# Revit family: LAMP_PUZZLE IND
name_source: partatom
category: Modelos genéricos
revit_build: Autodesk Revit 2015 (Build: 20140606_1530(x64)
units: mm (PartAtom-declared; Revit-internal decimal feet)

## types (32) — shared parameters
CRI = 80
Comentarios de tipo = Availability of tilting between -25º and 25º in both directions when placed in a project.
Dimensions = 140 x 140 x 139
Elevación por defecto = 1219 mm
Fabricante = LAMP
Gear = Electronic
Height = 139 mm  [stored 0.456037 ft]
Installation instructions = http://www.lamp.es
Insulation class = II
Lamp = COB LED
Last update = 24/07/2018
Luminaire type = Indoor - Recesses luminaire
MacAdam = 3
Manufacturer URL = http://www.lamp.es
Manufacturer country = Spain
Manufacturer name = LAMP
Model explanation = Availability of tilting between -25º and 25º in both directions when placed in a project.
Power Supply = 220-240V 50-60Hz
Product URL = http://www.lamp.es
Product datasheet = http://www.lamp.es
Protection rating = IP20
Type = COB PHILIPS

## per-type parameters (varying)
| type | Descripción | Efficacy | Finish | IEE | Initial color | Initial intensity | LED Lifetime | Material caja | Modelo | Photometric web file | Plum | Power | Product code | Weight |
| 1405LM 3000 BLACK FLOOD | PUZZLE G2 IND 1500 WW FL BK. | 145 lm/W | Matte black | A++ | 3000 K | 1405 lm | 50.000 L90 B10 | LAMP_Aluminio aro Puzzle BL | PU2RE115FL830NB | Aro exterior : 1405LM 3000 BLACK FLOOD | 10 W | 8 W | PU2RE115FL830NB | 1.09 kg |
| 1405LM 3000 WHITE FLOOD | PUZZLE G2 IND 1500 WW FL WH. | 145 lm/W | Matte white | A++ | 3000 K | 1405 lm | 50.000 L90 B10 | LAMP_Aluminio aro Puzzle WH | PU2RE115FL830NW | Aro exterior : 1405LM 3000 WHITE FLOOD | 10 W | 8 W | PU2RE115FL830NW | 1.09 kg |
| 1421LM 3000 BLACK MEDIUM FLOOD | PUZZLE G2 IND 1500 WW MFL BK. | 147 lm/W | Matte black | A++ | 3000 K | 1421 lm | 50.000 L90 B10 | LAMP_Aluminio aro Puzzle BL | PU2RE115MF830NB | Aro exterior : 1421LM 3000 BLACK MEDIUM FLOOD | 10 W | 8 W | PU2RE115MF830NB | 1.09 kg |
| 1421LM 3000 WHITE MEDIUM FLOOD | PUZZLE G2 IND 1500 WW MFL WH. | 147 lm/W | Matte white | A++ | 3000 K | 1421 lm | 50.000 L90 B10 | LAMP_Aluminio aro Puzzle WH | PU2RE115MF830NW | Aro exterior : 1421LM 3000 WHITE MEDIUM FLOOD | 10 W | 8 W | PU2RE115MF830NW | 1.09 kg |
| 1464LM 4000 BLACK FLOOD | PUZZLE G2 IND 1500 NW FL BK. | 151 lm/W | Matte black | A++ | 4000 K | 1464 lm | 50.000 L90 B10 | LAMP_Aluminio aro Puzzle BL | PU2RE115FL840NB | Aro exterior : 1464LM 4000 BLACK FLOOD | 10 W | 8 W | PU2RE115FL840NB | 1.09 kg |
| 1464LM 4000 WHITE FLOOD | PUZZLE G2 IND 1500 NW FL WH. | 151 lm/W | Matte white | A++ | 4000 K | 1464 lm | 50.000 L90 B10 | LAMP_Aluminio aro Puzzle WH | PU2RE115FL840NW | Aro exterior : 1464LM 4000 WHITE FLOOD | 10 W | 8 W | PU2RE115FL840NW | 1.09 kg |
| 1480LM 4000 BLACK MEDIUM FLOOD | PUZZLE G2 IND 1500 NW MFL BK. | 153 lm/W | Matte black | A++ | 4000 K | 1480 lm | 50.000 L90 B10 | LAMP_Aluminio aro Puzzle BL | PU2RE115MF840NB | Aro exterior : 1480LM 4000 BLACK MEDIUM FLOOD | 10 W | 8 W | PU2RE115MF840NB | 1.09 kg |
| 1480LM 4000 WHITE MEDIUM FLOOD | PUZZLE G2 IND 1500 NW MFL WH. | 153 lm/W | Matte white | A++ | 4000 K | 1480 lm | 50.000 L90 B10 | LAMP_Aluminio aro Puzzle WH | PU2RE115MF840NW | Aro exterior : 1480LM 4000 WHITE MEDIUM FLOOD | 10 W | 8 W | PU2RE115MF840NW | 1.09 kg |
| 2344LM 3000 BLACK FLOOD | PUZZLE G2 IND 2500 WW FL BK. | 124 lm/W | Matte black | A++ | 3000 K | 2344 lm | 50.000 L80 B10 | LAMP_Aluminio aro Puzzle BL | PU2RE125FL830NB | Aro exterior : 2344LM 3000 BLACK FLOOD | 19 W | 18 W | PU2RE125FL830NB | 1.09 kg |
| 2344LM 3000 WHITE FLOOD | PUZZLE G2 IND 2500 WW FL WH. | 124 lm/W | Matte white | A++ | 3000 K | 2344 lm | 50.000 L80 B10 | LAMP_Aluminio aro Puzzle WH | PU2RE125FL830NW | Aro exterior : 2344LM 3000 WHITE FLOOD | 19 W | 18 W | PU2RE125FL830NW | 1.09 kg |
| 2368LM 3000 BLACK MEDIUM FLOOD | PUZZLE G2 IND 2500 WW MFL BK. | 125 lm/W | Matte black | A++ | 3000 K | 2368 lm | 50.000 L80 B10 | LAMP_Aluminio aro Puzzle BL | PU2RE125MF830NB | Aro exterior : 2368LM 3000 BLACK MEDIUM FLOOD | 19 W | 18 W | PU2RE125MF830NB | 1.09 kg |
| 2368LM 3000 WHITE MEDIUM FLOOD | PUZZLE G2 IND 2500 WW MFL WH. | 125 lm/W | Matte white | A++ | 3000 K | 2368 lm | 50.000 L80 B10 | LAMP_Aluminio aro Puzzle WH | PU2RE125MF830NW | Aro exterior : 2368LM 3000 WHITE MEDIUM FLOOD | 19 W | 18 W | PU2RE125MF830NW | 1.09 kg |
| 2442LM 4000 BLACK FLOOD | PUZZLE G2 IND 2500 NW FL BK. | 129 lm/W | Matte black | A++ | 4000 K | 2442 lm | 50.000 L80 B10 | LAMP_Aluminio aro Puzzle BL | PU2RE125FL840NB | Aro exterior : 2442LM 4000 BLACK FLOOD | 19 W | 18 W | PU2RE125FL840NB | 1.09 kg |
| 2442LM 4000 WHITE FLOOD | PUZZLE G2 IND 2500 NW FL WH. | 129 lm/W | Matte white | A++ | 4000 K | 2442 lm | 50.000 L80 B10 | LAMP_Aluminio aro Puzzle WH | PU2RE125FL840NW | Aro exterior : 2442LM 4000 WHITE FLOOD | 19 W | 18 W | PU2RE125FL840NW | 1.09 kg |
| 2466LM 4000 BLACK MEDIUM FLOOD | PUZZLE G2 IND 2500 NW MFL BK. | 131 lm/W | Matte black | A++ | 4000 K | 2466 lm | 50.000 L80 B10 | LAMP_Aluminio aro Puzzle BL | PU2RE125MF840NB | Aro exterior : 2466LM 4000 BLACK MEDIUM FLOOD | 19 W | 18 W | PU2RE125MF840NB | 1.09 kg |
| 2466LM 4000 WHITE MEDIUM FLOOD | PUZZLE G2 IND 2500 NW MFL WH. | 131 lm/W | Matte white | A++ | 4000 K | 2466 lm | 50.000 L80 B10 | LAMP_Aluminio aro Puzzle WH | PU2RE125MF840NW | Aro exterior : 2466LM 4000 WHITE MEDIUM FLOOD | 19 W | 18 W | PU2RE125MF840NW | 1.09 kg |
| 3197LM 3000 BLACK FLOOD | PUZZLE G2 IND 3500 WW FL BK. | 97 lm/W | Matte black | A+ | 3000 K | 3197 lm | 50.000 L70 B10 | LAMP_Aluminio aro Puzzle BL | PU2RE135FL830NB | Aro exterior : 3197LM 3000 BLACK FLOOD | 33 W | 27 W | PU2RE135FL830NB | 1.14 kg |
| 3197LM 3000 WHITE FLOOD | PUZZLE G2 IND 3500 WW FL WH. | 97 lm/W | Matte white | A+ | 3000 K | 3197 lm | 50.000 L70 B10 | LAMP_Aluminio aro Puzzle WH | PU2RE135FL830NW | Aro exterior : 3197LM 3000 WHITE FLOOD | 33 W | 27 W | PU2RE135FL830NW | 1.14 kg |
| 3229LM 3000 BLACK MEDIUM FLOOD | PUZZLE G2 IND 3500 WW MFL BK. | 98 lm/W | Matte black | A+ | 3000 K | 3229 lm | 50.000 L70 B10 | LAMP_Aluminio aro Puzzle BL | PU2RE135MF830NB | Aro exterior : 3229LM 3000 BLACK MEDIUM FLOOD | 33 W | 27 W | PU2RE135MF830NB | 1.14 kg |
| 3229LM 3000 WHITE MEDIUM FLOOD | PUZZLE G2 IND 3500 WW MFL WH. | 98 lm/W | Matte white | A+ | 3000 K | 3229 lm | 50.000 L70 B10 | LAMP_Aluminio aro Puzzle WH | PU2RE135MF830NW | Aro exterior : 3229LM 3000 WHITE MEDIUM FLOOD | 33 W | 27 W | PU2RE135MF830NW | 1.14 kg |
| 3330LM 4000 BLACK FLOOD | PUZZLE G2 IND 3500 NW FL BK. | 101 lm/W | Matte black | A+ | 4000 K | 3330 lm | 50.000 L70 B10 | LAMP_Aluminio aro Puzzle BL | PU2RE135FL840NB | Aro exterior : 3330LM 4000 BLACK FLOOD | 33 W | 27 W | PU2RE135FL840NB | 1.14 kg |
| 3330LM 4000 WHITE FLOOD | PUZZLE G2 IND 3500 NW FL WH. | 101 lm/W | Matte white | A+ | 4000 K | 3330 lm | 50.000 L70 B10 | LAMP_Aluminio aro Puzzle WH | PU2RE135FL840NW | Aro exterior : 3330LM 4000 WHITE FLOOD | 33 W | 27 W | PU2RE135FL840NW | 1.14 kg |
| 3363LM 4000 BLACK MEDIUM FLOOD | PUZZLE G2 IND 3500 NW MFL BK. | 102 lm/W | Matte black | A+ | 4000 K | 3363 lm | 50.000 L70 B10 | LAMP_Aluminio aro Puzzle BL | PU2RE135MF840NB | Aro exterior : 3363LM 4000 BLACK MEDIUM FLOOD | 33 W | 27 W | PU2RE135MF840NB | 1.14 kg |
| 3363LM 4000 WHITE MEDIUM FLOOD | PUZZLE G2 IND 3500 NW MFL WH. | 102 lm/W | Matte white | A+ | 4000 K | 3363 lm | 50.000 L70 B10 | LAMP_Aluminio aro Puzzle WH | PU2RE135MF840NW | Aro exterior : 3363LM 4000 WHITE MEDIUM FLOOD | 33 W | 27 W | PU2RE135MF840NW | 1.14 kg |
| 4051LM 3000 BLACK MEDIUM FLOOD | PUZZLE G2 IND 4600 WW MFL BK. | 106 lm/W | Matte black | A+ | 3000 K | 4051 lm | 50.000 L80 B10 | LAMP_Aluminio aro Puzzle BL | PU2RE145MF830NB | Aro exterior : 4051LM 3000 BLACK MEDIUM FLOOD | 38 W | 33 W | PU2RE145MF830NB | 1.22 kg |
| 4051LM 3000 WHITE MEDIUM FLOOD | PUZZLE G2 IND 4600 WW MFL WH. | 106 lm/W | Matte white | A+ | 3000 K | 4051 lm | 50.000 L80 B10 | LAMP_Aluminio aro Puzzle WH | PU2RE145MF830NW | Aro exterior : 4051LM 3000 WHITE MEDIUM FLOOD | 38 W | 33 W | PU2RE145MF830NW | 1.22 kg |
| 4137LM 3000 BLACK FLOOD | PUZZLE G2 IND 4600 WW FL BK. | 108 lm/W | Matte black | A+ | 3000 K | 4137 lm | 50.000 L80 B10 | LAMP_Aluminio aro Puzzle BL | PU2RE145FL830NB | Aro exterior : 4137LM 3000 BLACK FLOOD | 38 W | 33 W | PU2RE145FL830NB | 1.22 kg |
| 4137LM 3000 WHITE FLOOD | PUZZLE G2 IND 4600 WW FL WH. | 108 lm/W | Matte white | A+ | 3000 K | 4137 lm | 50.000 L80 B10 | LAMP_Aluminio aro Puzzle WH | PU2RE145FL830NW | Aro exterior : 4137LM 3000 WHITE FLOOD | 38 W | 33 W | PU2RE145FL830NW | 1.22 kg |
| 4220LM 4000 BLACK MEDIUM FLOOD | PUZZLE G2 IND 4600 NW MFL BK. | 111 lm/W | Matte black | A+ | 4000 K | 4220 lm | 50.000 L80 B10 | LAMP_Aluminio aro Puzzle BL | PU2RE145MF840NB | Aro exterior : 4220LM 4000 BLACK MEDIUM FLOOD | 38 W | 33 W | PU2RE145MF840NB | 1.22 kg |
| 4220LM 4000 WHITE MEDIUM FLOOD | PUZZLE G2 IND 4600 NW MFL WH. | 111 lm/W | Matte white | A+ | 4000 K | 4220 lm | 50.000 L80 B10 | LAMP_Aluminio aro Puzzle WH | PU2RE145MF840NW | Aro exterior : 4220LM 4000 WHITE MEDIUM FLOOD | 38 W | 33 W | PU2RE145MF840NW | 1.22 kg |
| 4309LM 4000 BLACK FLOOD | PUZZLE G2 IND 4600 NW FL BK. | 113 lm/W | Matte black | A+ | 4000 K | 4309 lm | 50.000 L80 B10 | LAMP_Aluminio aro Puzzle BL | PU2RE145FL840NB | Aro exterior : 4309LM 4000 BLACK FLOOD | 38 W | 33 W | PU2RE145FL840NB | 1.22 kg |
| 4309LM 4000 WHITE FLOOD | PUZZLE G2 IND 4600 NW FL WH. | 113 lm/W | Matte white | A+ | 4000 K | 4309 lm | 50.000 L80 B10 | LAMP_Aluminio aro Puzzle WH | PU2RE145FL840NW | Aro exterior : 4309LM 4000 WHITE FLOOD | 38 W | 33 W | PU2RE145FL840NW | 1.22 kg |

note: [stored X ft] marks values corroborated as IEEE doubles in the binary element streams (Revit-internal decimal feet)
